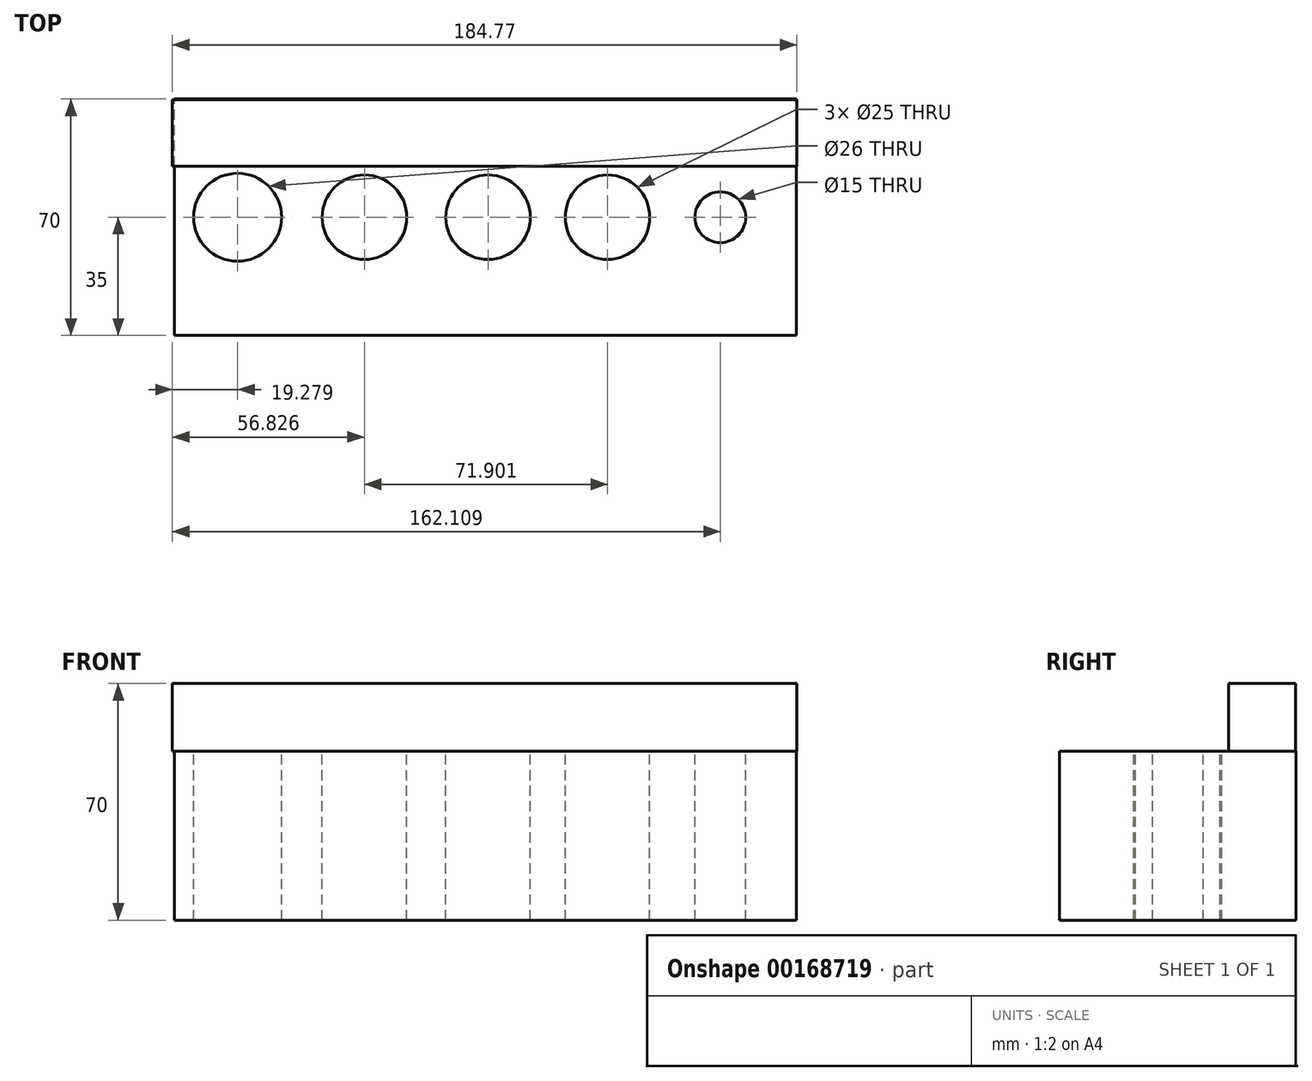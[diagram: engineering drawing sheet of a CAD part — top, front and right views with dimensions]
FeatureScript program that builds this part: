
annotation { "Feature Type Name" : "Feature", "Feature Type Description" : "" }
export const myFeature = defineFeature(function(context is Context, id is Id, definition is map)
    precondition{}
    {
        {
            var Q0;
            Q0=qCreatedBy(makeId("Top.planeOp"),FACE);
            var sketch = newSketch(context, id + "F0", { "sketchPlane" : qUnion([Q0])});
            skLineSegment(sketch, "E0.bottom", {"start": v(66.33, -35) * mm, "end": v(-117.66, -35) * mm});
            skLineSegment(sketch, "E0.top", {"start": v(66.33, 35) * mm, "end": v(-117.66, 35) * mm});
            skLineSegment(sketch, "E0.right", {"start": v(-117.66, -35) * mm, "end": v(-117.66, 35) * mm});
            skPoint(sketch, "E0.middle", {"position": v(0, 0) * mm});
            skCircle(sketch, "E1", {"center": v(-99.01, 0) * mm, "radius": 13 * mm});
            skCircle(sketch, "E2", {"center": v(-61.46, 0) * mm, "radius": 12.5 * mm});
            skCircle(sketch, "E3", {"center": v(-24.9, 0) * mm, "radius": 12.5 * mm});
            skCircle(sketch, "E4", {"center": v(10.44, 0) * mm, "radius": 12.5 * mm});
            skCircle(sketch, "E5", {"center": v(43.82, 0) * mm, "radius": 7.5 * mm});
            skLineSegment(sketch, "E6", {"start": v(66.33, -35) * mm, "end": v(66.33, 35) * mm});
            skSolve(sketch);
        }
        {
            var Q0;
            Q0=makeQuery(id+"F0.imprint","IMPRINT",FACE,{"disambiguationData":[TD([[makeQuery(id+"F0.imprint","IMPRINT",EDGE,{"derivedFrom":sQuery(id+"F0.wireOp",EDGE,"E0.bottom")}),-1.0]])]});
            extrude(context, id + "F1", {"entities" : qUnion([Q0]), "endBound" : BoundingType.SYMMETRIC, "oppositeDirection" : true, "depth" : 50 * mm});
        }
        {
            var Q0;
            Q0=makeQuery(id+"F1.opExtrude","CAP_FACE",FACE,{"disambiguationData":[OSD([sQuery(id+"F0.wireOp",EDGE,"E0.bottom"),sQuery(id+"F0.wireOp",EDGE,"E0.top"),sQuery(id+"F0.wireOp",EDGE,"E0.right"),sQuery(id+"F0.wireOp",EDGE,"E1"),sQuery(id+"F0.wireOp",EDGE,"E2"),sQuery(id+"F0.wireOp",EDGE,"E3"),sQuery(id+"F0.wireOp",EDGE,"E4"),sQuery(id+"F0.wireOp",EDGE,"E5"),sQuery(id+"F0.wireOp",EDGE,"E6")])],"isStart":true});
            var sketch = newSketch(context, id + "F2", { "sketchPlane" : qUnion([Q0])});
            skSolve(sketch);
        }
        {
            var Q0;
            Q0=makeQuery(id+"F2.imprint","IMPRINT",FACE,{"disambiguationData":[TD([[makeQuery(id+"F2.imprint","IMPRINT",EDGE,{"derivedFrom":makeQuery(id+"F1.opExtrude","CAP_EDGE",EDGE,{"disambiguationData":[OSD([sQuery(id+"F0.wireOp",EDGE,"E0.bottom")])],"isStart":true})}),-1.0]])]});
            var sketch = newSketch(context, id + "F3", { "sketchPlane" : qUnion([Q0])});
            skLineSegment(sketch, "E7.bottom", {"start": v(-118.3, 34.8) * mm, "end": v(66.48, 34.8) * mm});
            skLineSegment(sketch, "E7.top", {"start": v(-118.3, 15.07) * mm, "end": v(66.48, 15.07) * mm});
            skLineSegment(sketch, "E7.left", {"start": v(-118.3, 34.8) * mm, "end": v(-118.3, 15.07) * mm});
            skLineSegment(sketch, "E7.right", {"start": v(66.48, 34.8) * mm, "end": v(66.48, 15.07) * mm});
            skSolve(sketch);
        }
        {
            var Q0;
            Q0 = qSketchRegion(id + "F3", true);
            extrude(context, id + "F4", {"entities" : qUnion([Q0]), "operationType" : NewBodyOperationType.ADD, "depth" : 20 * mm});
        }
    });
